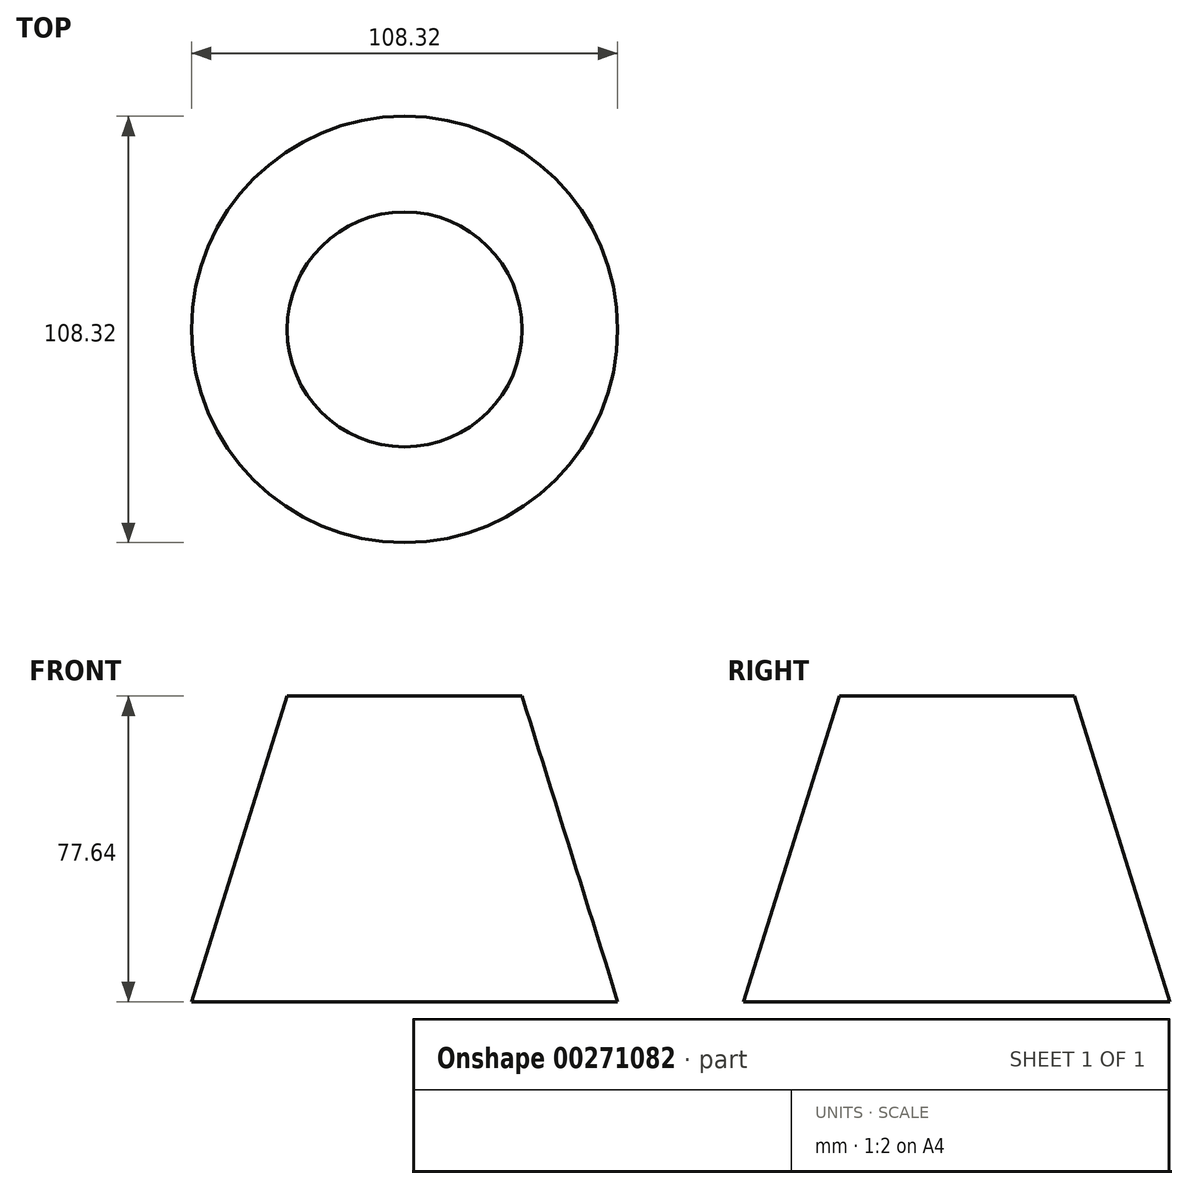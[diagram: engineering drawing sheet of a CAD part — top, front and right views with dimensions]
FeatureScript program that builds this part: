
annotation { "Feature Type Name" : "Feature", "Feature Type Description" : "" }
export const myFeature = defineFeature(function(context is Context, id is Id, definition is map)
    precondition{}
    {
        {
            var Q0;
            Q0=qCreatedBy(makeId("Front.planeOp"),FACE);
            var sketch = newSketch(context, id + "F0", { "sketchPlane" : qUnion([Q0])});
            skLineSegment(sketch, "E0", {"start": v(0, -38.68) * mm, "end": v(54.16, -38.68) * mm});
            skLineSegment(sketch, "E1", {"start": v(0, -38.68) * mm, "end": v(0, 38.96) * mm});
            skLineSegment(sketch, "E2", {"start": v(0, 38.96) * mm, "end": v(29.84, 38.96) * mm});
            skLineSegment(sketch, "E3", {"start": v(29.84, 38.96) * mm, "end": v(54.16, -38.68) * mm});
            skLineSegment(sketch, "E4", {"start": v(0, 54.71) * mm, "end": v(0, -62.45) * mm, "construction": true});
            skSolve(sketch);
        }
        {
            var Q0;
            Q0 = qSketchRegion(id + "F0", true);
            var Q1;
            Q1=sQuery(id+"F0.wireOp",EDGE,"E4");
            revolve(context, id + "F1", {"entities" : qUnion([Q0]), "axis" : qUnion([Q1]), "revolveType" : RevolveType.FULL});
        }
    });
